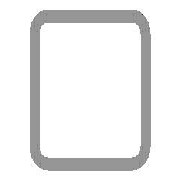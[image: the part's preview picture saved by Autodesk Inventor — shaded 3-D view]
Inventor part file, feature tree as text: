
AUTODESK INVENTOR PART (.ipt)
format: ipt  version: 2025 (Build 290162010, 162A)  size: 133,120 bytes
history: native  units: mm (DEFAULTED — no unit token found)
features: other x4, sketch x1, plane x1
ambient origin geometry x8: Origin, YZ Plane, XZ Plane, XY Plane, X Axis, Y Axis, Z Axis, Center Point
bodies: Solid1 (feature_tree), Body (feature_tree)
feature tree (6):
  parser-record x1  (decoder bookkeeping rows leaked as tree rows — omitted from the tree; the rows remain in map.json)
  other  "Driven Length"
  other  "Start Plane"
  other  "End Plane"
  sketch  "Sketch3"  dims[d3=5400.0mm d4=0.0mm d7=6.0mm d9=100.0mm d11=100.0mm d12=3.0mm d13=-0.0mm d14=5400.0mm d15=50.0mm d16=50.0mm d17=90.0deg d18=5400.0mm]
  plane  "Work Plane3"
